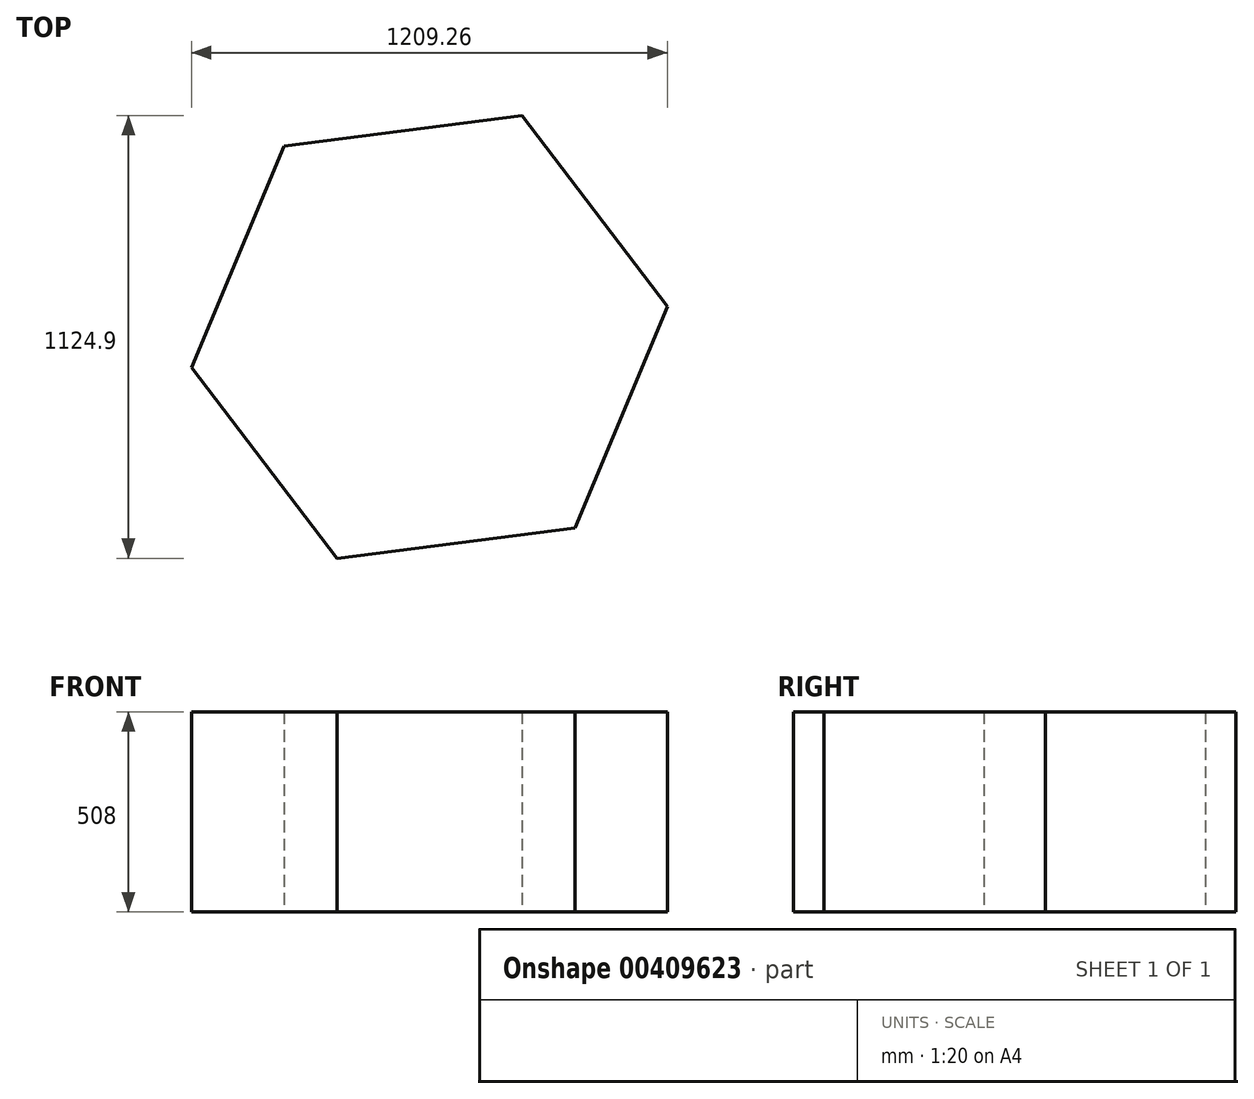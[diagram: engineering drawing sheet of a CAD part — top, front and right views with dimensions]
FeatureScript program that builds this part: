
annotation { "Feature Type Name" : "Feature", "Feature Type Description" : "" }
export const myFeature = defineFeature(function(context is Context, id is Id, definition is map)
    precondition{}
    {
        {
            var Q0;
            Q0=qCreatedBy(makeId("Top.planeOp"),FACE);
            var sketch = newSketch(context, id + "F0", { "sketchPlane" : qUnion([Q0])});
            skCircle(sketch, "E0.cCircle", {"center": v(0, 0) * mm, "radius": 527.93 * mm, "construction": true});
            skLineSegment(sketch, "E0.0", {"start": v(369.56, -484.8) * mm, "end": v(-235.07, -562.45) * mm});
            skLineSegment(sketch, "E0.1", {"start": v(-235.07, -562.45) * mm, "end": v(-604.63, -77.65) * mm});
            skLineSegment(sketch, "E0.2", {"start": v(-604.63, -77.65) * mm, "end": v(-369.56, 484.8) * mm});
            skLineSegment(sketch, "E0.3", {"start": v(-369.56, 484.8) * mm, "end": v(235.07, 562.45) * mm});
            skLineSegment(sketch, "E0.4", {"start": v(235.07, 562.45) * mm, "end": v(604.63, 77.65) * mm});
            skLineSegment(sketch, "E0.5", {"start": v(604.63, 77.65) * mm, "end": v(369.56, -484.8) * mm});
            skPoint(sketch, "E0.0.midPoint", {"position": v(67.25, -523.63) * mm});
            skSolve(sketch);
        }
        {
            var Q0;
            Q0 = qSketchRegion(id + "F0", true);
            extrude(context, id + "F1", {"entities" : qUnion([Q0]), "depth" : 508 * mm});
        }
    });
